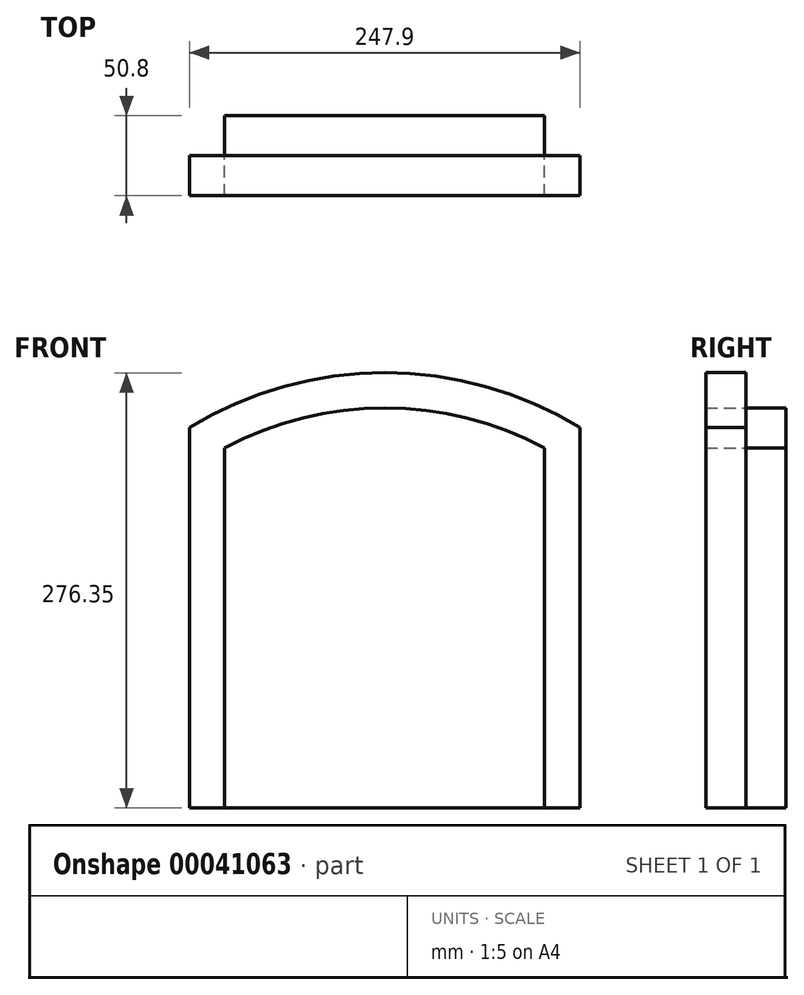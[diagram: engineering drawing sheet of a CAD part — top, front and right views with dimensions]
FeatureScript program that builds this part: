
annotation { "Feature Type Name" : "Feature", "Feature Type Description" : "" }
export const myFeature = defineFeature(function(context is Context, id is Id, definition is map)
    precondition{}
    {
        {
            var Q0;
            Q0=qCreatedBy(makeId("Front.planeOp"),FACE);
            var sketch = newSketch(context, id + "F0", { "sketchPlane" : qUnion([Q0])});
            skLineSegment(sketch, "E0.rect.bottom", {"start": v(101.6, 114.3) * mm, "end": v(-101.6, 114.3) * mm});
            skLineSegment(sketch, "E0.rect.top", {"start": v(101.6, -114.3) * mm, "end": v(-101.6, -114.3) * mm});
            skLineSegment(sketch, "E0.rect.left", {"start": v(101.6, 114.3) * mm, "end": v(101.6, -114.3) * mm});
            skLineSegment(sketch, "E0.rect.right", {"start": v(-101.6, 114.3) * mm, "end": v(-101.6, -114.3) * mm});
            skPoint(sketch, "E0.rect.middle", {"position": v(0, 0) * mm});
            skArc(sketch, "E1", {"start": v(101.6, 114.3) * mm, "mid": v(0, 139.7) * mm, "end": v(-101.6, 114.3) * mm});
            skSolve(sketch);
        }
        {
            var Q0;
            Q0 = qSketchRegion(id + "F0", true);
            extrude(context, id + "F1", {"entities" : qUnion([Q0]), "depth" : 25.4 * mm});
        }
        {
            var Q0;
            Q0=makeQuery(id+"F1.opExtrude","CAP_FACE",FACE,{"disambiguationData":[OSD([sQuery(id+"F0.wireOp",EDGE,"E0.rect.top"),sQuery(id+"F0.wireOp",EDGE,"E0.rect.left"),sQuery(id+"F0.wireOp",EDGE,"E0.rect.right"),sQuery(id+"F0.wireOp",EDGE,"E1")])],"isStart":false});
            var sketch = newSketch(context, id + "F2", { "sketchPlane" : qUnion([Q0])});
            skLineSegment(sketch, "E2.0", {"start": v(-123.95, 127.27) * mm, "end": v(-123.95, -114.3) * mm});
            skArc(sketch, "E2.1", {"start": v(123.95, 127.27) * mm, "mid": v(0, 162.05) * mm, "end": v(-123.95, 127.27) * mm});
            skLineSegment(sketch, "E2.2", {"start": v(123.95, 127.27) * mm, "end": v(123.95, -114.3) * mm});
            skLineSegment(sketch, "E3", {"start": v(-123.95, -114.3) * mm, "end": v(123.95, -114.3) * mm});
            skLineSegment(sketch, "E4.0", {"start": v(-101.6, 114.3) * mm, "end": v(-101.6, -114.3) * mm});
            skArc(sketch, "E4.1", {"start": v(101.6, 114.3) * mm, "mid": v(0, 139.7) * mm, "end": v(-101.6, 114.3) * mm});
            skLineSegment(sketch, "E4.2", {"start": v(101.6, 114.3) * mm, "end": v(101.6, -114.3) * mm});
            skSolve(sketch);
        }
        {
            var Q0;
            {var subQ4=sQuery(id+"F2.wireOp",EDGE,"E2.0");Q0=makeQuery(id+"F2.imprint","IMPRINT",FACE,{"disambiguationData":[TD([[makeQuery(id+"F2.imprint","IMPRINT",EDGE,{"derivedFrom":subQ4}),1.0]])]});}
            extrude(context, id + "F3", {"entities" : qUnion([Q0]), "operationType" : NewBodyOperationType.ADD, "depth" : 25.4 * mm});
        }
    });
